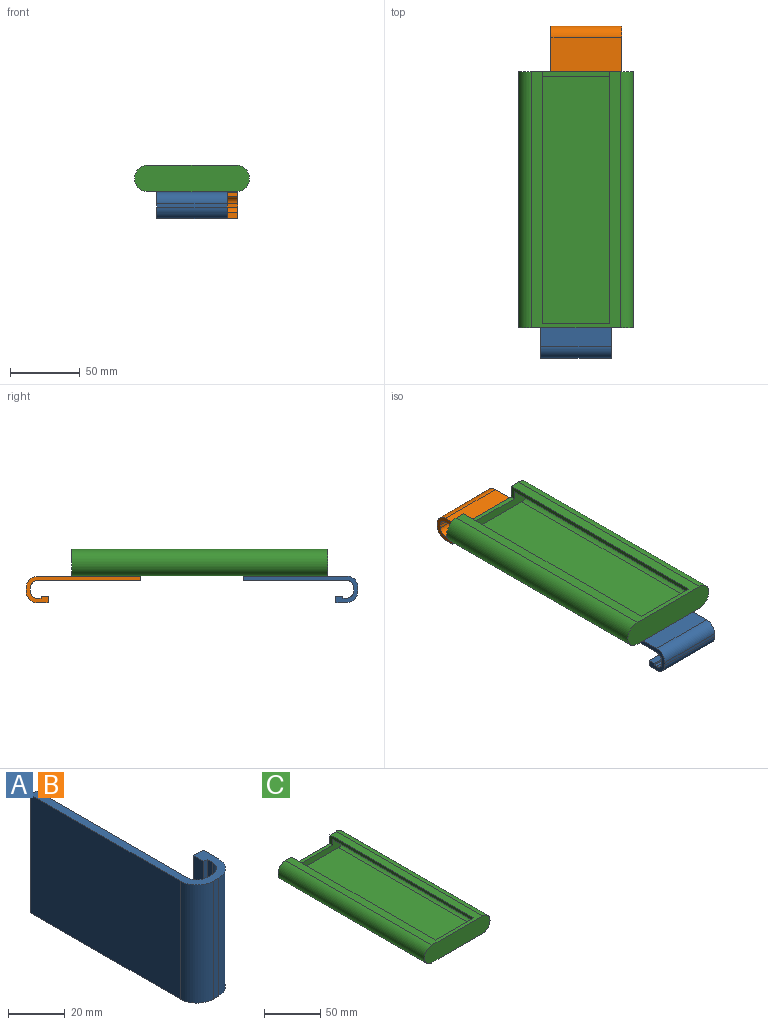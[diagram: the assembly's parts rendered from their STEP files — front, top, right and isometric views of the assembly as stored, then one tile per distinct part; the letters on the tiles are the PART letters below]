
ASSEMBLY  parts=3 mates=1
PART A: 16 faces, bbox 19.1x82.6x50.8 mm
  f0: plane 50.8x7.62mm, normal (1,0,0), area 387.1mm2, adj f1,f11,f12,f13
  f1: plane 50.8x4.7mm, normal (0,1,0), area 238.7mm2, adj f0,f12,f13,f15
  f2: plane 50.8x2.54mm, normal (-1,0,0), area 129mm2, adj f3,f12,f13,f14
  f3: cylinder r=5.08mm len=50.8mm, axis (0,0,-1), area 405.4mm2, adj f2,f4,f12,f13
  f4: plane 50.8x2.54mm, normal (0,1,0), area 129mm2, adj f3,f5,f12,f13
  f5: cylinder r=5.08mm len=50.8mm, axis (0,0,-1), area 405.4mm2, adj f4,f6,f12,f13
  f6: plane 74.3x50.8mm, normal (1,0,0), area 3774.2mm2, adj f5,f7,f12,f13
  f7: plane 50.8x3.18mm, normal (0,1,0), area 161.3mm2, adj f6,f8,f12,f13
  f8: plane 74.3x50.8mm, normal (-1,0,0), area 3774.2mm2, adj f7,f9,f12,f13
  f9: cylinder r=8.26mm len=50.8mm, axis (0,0,-1), area 658.7mm2, adj f8,f10,f12,f13
  f10: plane 50.8x2.54mm, normal (0,-1,0), area 129mm2, adj f9,f11,f12,f13
  f11: cylinder r=8.26mm len=50.8mm, axis (0,0,-1), area 658.7mm2, adj f0,f10,f12,f13
  f12: plane 82.55x19.05mm, normal (0,0,1), area 342.4mm2, adj f0,f1,f2,f3,f4,f5,f6,f7
  f13: plane 82.55x19.05mm, normal (0,0,-1), area 342.4mm2, adj f0,f1,f2,f3,f4,f5,f6,f7
  f14: plane 50.8x1.52mm, normal (0,-1,0), area 77.4mm2, adj f2,f12,f13,f15
  f15: plane 50.8x5.08mm, normal (-1,0,0), area 258.1mm2, adj f1,f12,f13,f14
PART B: same geometry as A
PART C: 16 faces, bbox 82.6x184.2x19.1 mm
  f0: plane 177.8x63.5mm, normal (0,0,1), area 11290.3mm2, adj f1,f10,f12,f13
  f1: cylinder r=6.35mm len=177.8mm, axis (0,1,0), area 3547mm2, adj f0,f2,f12,f13
  f2: plane 177.8x7.62mm, normal (0,0,-1), area 1354.8mm2, adj f1,f3,f12,f13
  f3: plane 180.98x9.53mm, normal (1,0,0), area 594.8mm2, adj f2,f7,f12,f13,f14,f15
  f4: cylinder r=9.53mm len=184.15mm, axis (0,1,0), area 5510.4mm2, adj f5,f7,f11,f15
  f5: plane 184.15x63.5mm, normal (0,0,-1), area 11693.5mm2, adj f4,f6,f11,f15
  f6: cylinder r=9.53mm len=184.15mm, axis (0,1,0), area 5510.4mm2, adj f5,f7,f11,f15
  f7: plane 184.15x63.5mm, normal (0,0,1), area 2959.7mm2, adj f3,f4,f6,f8,f11,f12,f15
  f8: plane 180.98x9.53mm, normal (-1,0,0), area 594.8mm2, adj f7,f9,f12,f13,f14,f15
  f9: plane 177.8x7.62mm, normal (0,0,-1), area 1354.8mm2, adj f8,f10,f12,f13
  f10: cylinder r=6.35mm len=177.8mm, axis (0,1,0), area 3547mm2, adj f0,f9,f12,f13
  f11: plane 82.55x19.05mm, normal (0,-1,0), area 1494.7mm2, adj f4,f5,f6,f7
  f12: plane 76.2x15.88mm, normal (0,1,0), area 1086.4mm2, adj f0,f1,f2,f3,f7,f8,f9,f10
  f13: plane 76.2x12.7mm, normal (0,-1,0), area 626.7mm2, adj f0,f1,f2,f3,f8,f9,f10,f14
  f14: plane 48.26x3.18mm, normal (0,0,1), area 153.2mm2, adj f3,f8,f13,f15
  f15: plane 82.55x19.05mm, normal (0,1,0), area 1035mm2, adj f3,f4,f5,f6,f7,f8,f14
PLACE A rot(axis=(0,1,0),90deg) t=(28,-87.77,-64.06)mm
PLACE B rot(axis=(-0.71,0,0.71),180deg) t=(86.22,-14.09,-64.26)mm
PLACE C t=(12.14,32.43,-63.78)mm
MATE parallel A.f8 <-> C.f5  axis (0,0,1) through (53.4,-124.92,-64.06)mm
